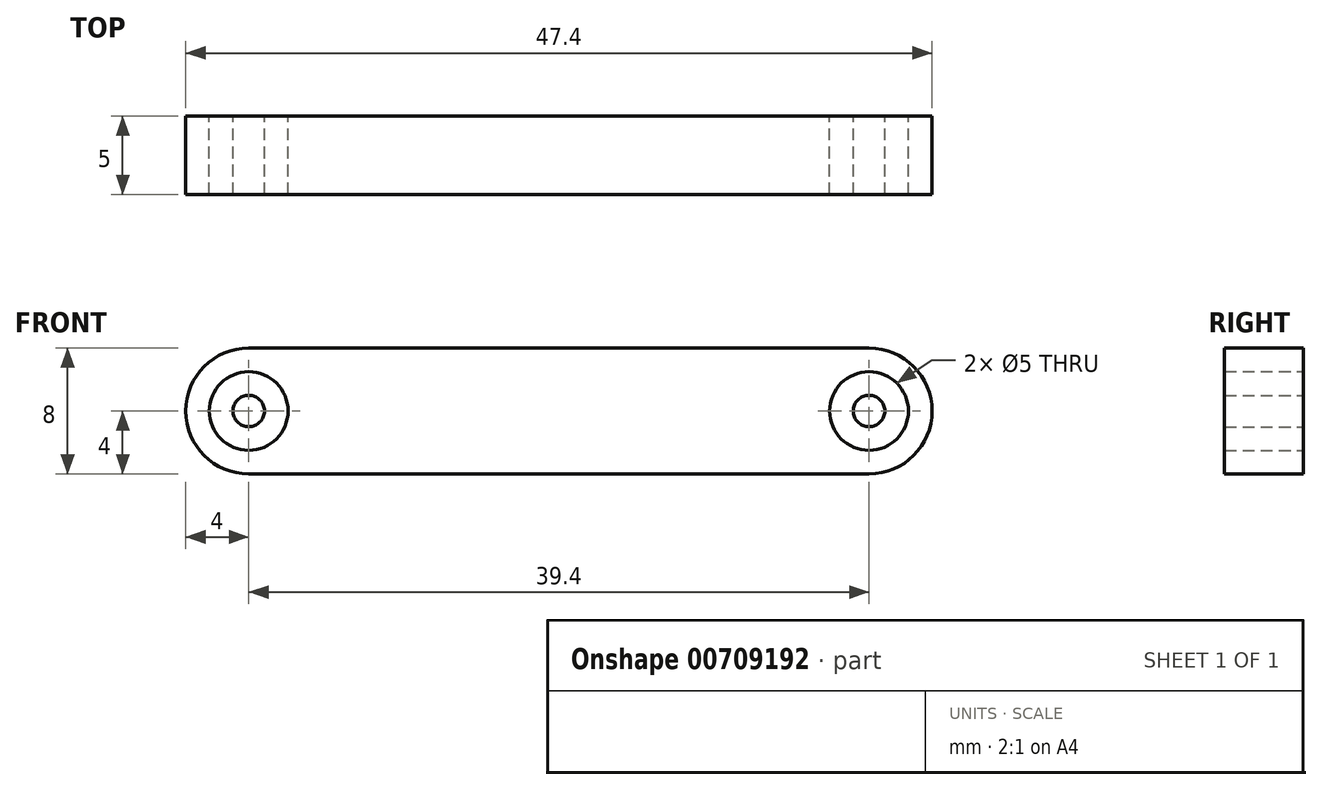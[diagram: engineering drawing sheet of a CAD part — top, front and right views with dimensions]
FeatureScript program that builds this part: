
annotation { "Feature Type Name" : "Feature", "Feature Type Description" : "" }
export const myFeature = defineFeature(function(context is Context, id is Id, definition is map)
    precondition{}
    {
        {
            var Q0;
            Q0=qCreatedBy(makeId("Front.planeOp"),FACE);
            var sketch = newSketch(context, id + "F0", { "sketchPlane" : qUnion([Q0])});
            skArc(sketch, "E0", {"start": v(0, 4) * mm, "mid": v(-4, 0) * mm, "end": v(0, -4) * mm});
            skArc(sketch, "E1", {"start": v(39.4, -4) * mm, "mid": v(43.4, 0) * mm, "end": v(39.4, 4) * mm});
            skLineSegment(sketch, "E2", {"start": v(0, 4) * mm, "end": v(39.4, 4) * mm});
            skLineSegment(sketch, "E3", {"start": v(0, -4) * mm, "end": v(39.4, -4) * mm});
            skCircle(sketch, "E4", {"center": v(0, 0) * mm, "radius": 2.5 * mm});
            skCircle(sketch, "E5", {"center": v(0, 0) * mm, "radius": 1 * mm});
            skCircle(sketch, "E6", {"center": v(39.4, 0) * mm, "radius": 1 * mm});
            skCircle(sketch, "E7", {"center": v(39.4, 0) * mm, "radius": 2.5 * mm});
            skSolve(sketch);
        }
        {
            var Q0;
            Q0=makeQuery(id+"F0.imprint","IMPRINT",FACE,{"disambiguationData":[TD([[makeQuery(id+"F0.imprint","IMPRINT",EDGE,{"derivedFrom":sQuery(id+"F0.wireOp",EDGE,"E0")}),1.0]])]});
            var Q1;
            Q1=makeQuery(id+"F0.imprint","IMPRINT",FACE,{"disambiguationData":[TD([[makeQuery(id+"F0.imprint","IMPRINT",EDGE,{"derivedFrom":sQuery(id+"F0.wireOp",EDGE,"E5")}),1.0]])]});
            var Q2;
            Q2=makeQuery(id+"F0.imprint","IMPRINT",FACE,{"disambiguationData":[TD([[makeQuery(id+"F0.imprint","IMPRINT",EDGE,{"derivedFrom":sQuery(id+"F0.wireOp",EDGE,"E6")}),1.0]])]});
            extrude(context, id + "F1", {"entities" : qUnion([Q0, Q1, Q2]), "depth" : 5 * mm, "offsetDistance" : 25 * mm});
        }
    });
